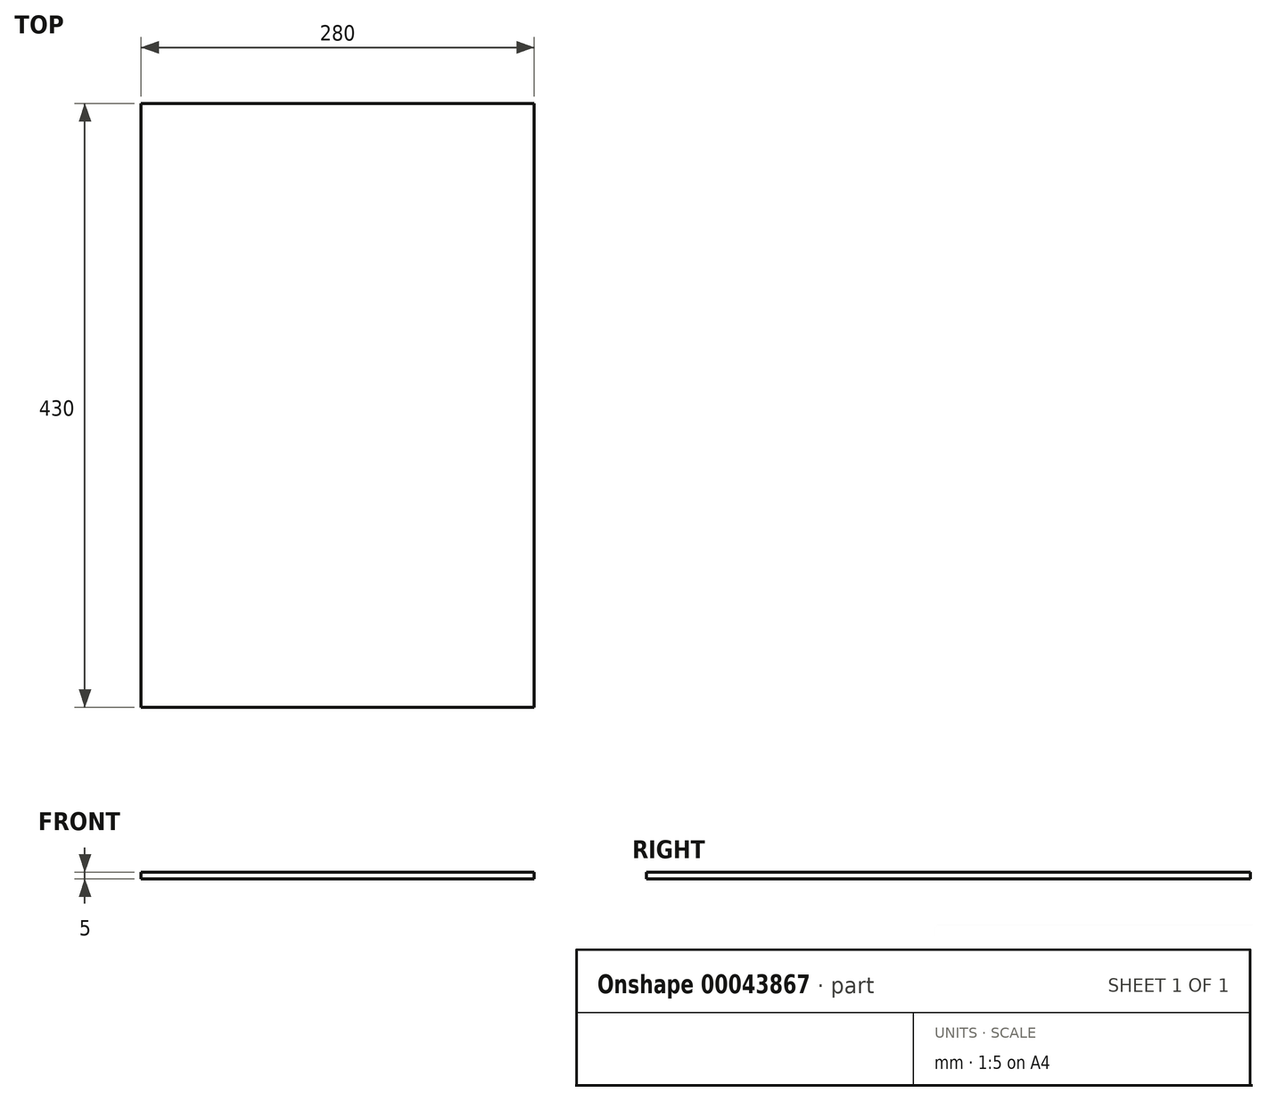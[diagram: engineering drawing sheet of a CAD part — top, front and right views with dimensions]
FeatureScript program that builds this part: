
annotation { "Feature Type Name" : "Feature", "Feature Type Description" : "" }
export const myFeature = defineFeature(function(context is Context, id is Id, definition is map)
    precondition{}
    {
        {
            var Q0;
            Q0=qCreatedBy(makeId("Top.planeOp"),FACE);
            var sketch = newSketch(context, id + "F0", { "sketchPlane" : qUnion([Q0])});
            skLineSegment(sketch, "E0.rect.bottom", {"start": v(-140, 215) * mm, "end": v(140, 215) * mm});
            skLineSegment(sketch, "E0.rect.top", {"start": v(-140, -215) * mm, "end": v(140, -215) * mm});
            skLineSegment(sketch, "E0.rect.left", {"start": v(-140, 215) * mm, "end": v(-140, -215) * mm});
            skLineSegment(sketch, "E0.rect.right", {"start": v(140, 215) * mm, "end": v(140, -215) * mm});
            skPoint(sketch, "E0.rect.middle", {"position": v(0, 0) * mm});
            skSolve(sketch);
        }
        {
            var Q0;
            Q0=makeQuery(id+"F0.imprint","IMPRINT",FACE,{"disambiguationData":[TD([[makeQuery(id+"F0.imprint","IMPRINT",EDGE,{"derivedFrom":sQuery(id+"F0.wireOp",EDGE,"E0.rect.bottom")}),-1.0]])]});
            extrude(context, id + "F1", {"entities" : qUnion([Q0]), "depth" : 5 * mm});
        }
    });
